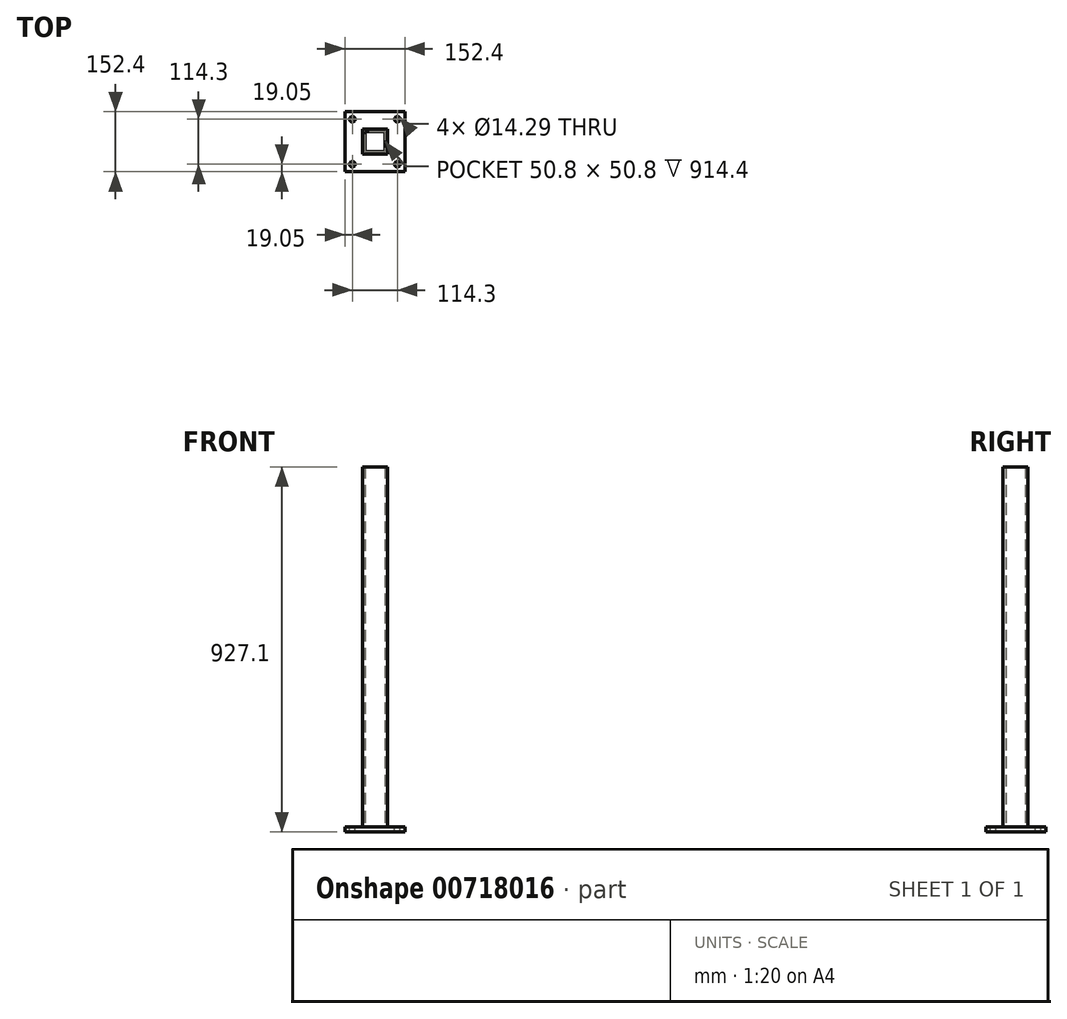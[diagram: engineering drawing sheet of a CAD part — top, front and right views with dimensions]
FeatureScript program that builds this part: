
annotation { "Feature Type Name" : "Feature", "Feature Type Description" : "" }
export const myFeature = defineFeature(function(context is Context, id is Id, definition is map)
    precondition{}
    {
        {
            var Q0;
            Q0=qCreatedBy(makeId("Front.planeOp"),FACE);
            var sketch = newSketch(context, id + "F0", { "sketchPlane" : qUnion([Q0])});
            skLineSegment(sketch, "E0", {"start": v(0, 0) * mm, "end": v(0, 914.4) * mm});
            skLineSegment(sketch, "E1", {"start": v(0, 914.4) * mm, "end": v(-63.5, 914.4) * mm});
            skLineSegment(sketch, "E2", {"start": v(-63.5, 914.4) * mm, "end": v(-63.5, 0) * mm});
            skLineSegment(sketch, "E3", {"start": v(-63.5, 0) * mm, "end": v(0, 0) * mm});
            skSolve(sketch);
        }
        {
            var Q0;
            Q0 = qSketchRegion(id + "F0", true);
            extrude(context, id + "F1", {"entities" : qUnion([Q0]), "depth" : 63.5 * mm, "offsetDistance" : 25.4 * mm});
        }
        {
            var Q0;
            Q0=makeQuery(id+"F1.opExtrude","SWEPT_FACE",FACE,{"disambiguationData":[OSD([sQuery(id+"F0.wireOp",EDGE,"E3")])]});
            var sketch = newSketch(context, id + "F2", { "sketchPlane" : qUnion([Q0])});
            skLineSegment(sketch, "E4", {"start": v(-57.15, 57.15) * mm, "end": v(-6.35, 57.15) * mm});
            skLineSegment(sketch, "E5", {"start": v(-6.35, 57.15) * mm, "end": v(-6.35, 6.35) * mm});
            skLineSegment(sketch, "E6", {"start": v(-57.15, 57.15) * mm, "end": v(-57.15, 6.35) * mm});
            skLineSegment(sketch, "E7", {"start": v(-57.15, 6.35) * mm, "end": v(-6.35, 6.35) * mm});
            skSolve(sketch);
        }
        {
            var Q0;
            Q0 = qSketchRegion(id + "F2", true);
            extrude(context, id + "F3", {"entities" : qUnion([Q0]), "operationType" : NewBodyOperationType.REMOVE, "endBound" : BoundingType.THROUGH_ALL, "oppositeDirection" : true, "depth" : 25.4 * mm, "offsetDistance" : 25.4 * mm});
        }
        {
            var Q0;
            Q0=makeQuery(id+"F1.opExtrude","SWEPT_FACE",FACE,{"disambiguationData":[OSD([sQuery(id+"F0.wireOp",EDGE,"E3")])]});
            var sketch = newSketch(context, id + "F4", { "sketchPlane" : qUnion([Q0])});
            skLineSegment(sketch, "E8", {"start": v(-63.5, 63.5) * mm, "end": v(-63.5, 107.95) * mm});
            skLineSegment(sketch, "E9", {"start": v(-63.5, 107.95) * mm, "end": v(-107.95, 107.95) * mm});
            skLineSegment(sketch, "E10", {"start": v(-107.95, 107.95) * mm, "end": v(-107.95, -44.45) * mm});
            skLineSegment(sketch, "E11", {"start": v(-107.95, -44.45) * mm, "end": v(44.45, -44.45) * mm});
            skLineSegment(sketch, "E12", {"start": v(44.45, -44.45) * mm, "end": v(44.45, 107.95) * mm});
            skLineSegment(sketch, "E13", {"start": v(44.45, 107.95) * mm, "end": v(-63.5, 107.95) * mm});
            skSolve(sketch);
        }
        {
            var Q0;
            Q0 = qSketchRegion(id + "F4", true);
            extrude(context, id + "F5", {"entities" : qUnion([Q0]), "operationType" : NewBodyOperationType.ADD, "depth" : 12.7 * mm, "offsetDistance" : 25.4 * mm});
        }
        {
            var Q0;
            {var subQ3=sQuery(id+"F0.wireOp",EDGE,"E0");var subQ4=sQuery(id+"F4.wireOp",EDGE,"E12");var subQ5=sQuery(id+"F4.wireOp",EDGE,"E13");var subQ6=sQuery(id+"F4.wireOp",EDGE,"E9");var subQ7=sQuery(id+"F4.wireOp",EDGE,"E10");var subQ8=sQuery(id+"F4.wireOp",EDGE,"E11");Q0=makeQuery(id+"F5.boolean.opBoolean","SPLIT",FACE,{"disambiguationData":[TD([makeQuery(id+"F1.opExtrude","SWEPT_FACE",FACE,{"disambiguationData":[OSD([subQ3])]})])],"derivedFrom":makeQuery(id+"F5.opExtrude","CAP_FACE",FACE,{"disambiguationData":[OSD([subQ6,subQ7,subQ8,subQ4,subQ5])],"isStart":true})});}
            var sketch = newSketch(context, id + "F6", { "sketchPlane" : qUnion([Q0])});
            skLineSegment(sketch, "E14", {"start": v(-107.95, 44.45) * mm, "end": v(-107.95, 25.4) * mm});
            skLineSegment(sketch, "E15", {"start": v(-107.95, 25.4) * mm, "end": v(30.17, 25.4) * mm});
            skLineSegment(sketch, "E16", {"start": v(-107.95, -88.9) * mm, "end": v(44.45, -88.9) * mm});
            skCircle(sketch, "E17", {"center": v(-88.9, -88.9) * mm, "radius": 7.14 * mm});
            skCircle(sketch, "E18", {"center": v(-88.9, 25.4) * mm, "radius": 7.14 * mm});
            skCircle(sketch, "E19", {"center": v(25.4, 25.4) * mm, "radius": 7.14 * mm});
            skCircle(sketch, "E20", {"center": v(25.4, -88.9) * mm, "radius": 7.14 * mm});
            skSolve(sketch);
        }
        {
            var Q0;
            Q0 = qSketchRegion(id + "F6", true);
            extrude(context, id + "F7", {"entities" : qUnion([Q0]), "operationType" : NewBodyOperationType.REMOVE, "oppositeDirection" : true, "depth" : 25.4 * mm, "offsetDistance" : 25.4 * mm});
        }
    });
